# Revit family: Plymold-Essentials-Recycle_Receptacle-
name_source: partatom
category: Furniture
units: mm (PartAtom-declared; Revit-internal decimal feet)

## family parameters
Always vertical = Yes
Cut with Voids When Loaded = No
OmniClass Number = 23.40.20.00
OmniClass Title = General Furniture and Specialties
Render Appearance Source = Family Geometry
Room Calculation Point = No
Shared = No
Work Plane-Based = No

## types (1)
- 80140
    Assembly Code = E2020200
    BACK MATERIAL = PLY - Natural Maple Horizontal
    Brand = Receptacle
    Cost = 0 $
    DIVIDER MATERIAL = PLY - Natural Maple Vertical
    DOOR MATERIAL = PLY - Natural Maple Vertical
    Default Elevation = 0"
    Depth = 16 3/4"
    Description = Three Stream Recycle Receptacle - 49"W x 16 3/4"D x 42"H
    EDGE HORIZONTAL MATERIAL = PLY - Natural Maple Horizontal
    EDGE MATERIAL = PLY - Plastic Black
    EDGE VERTICAL MATERIAL = PLY - Natural Maple Vertical
    FRONT MATERIAL = PLY - Natural Maple Horizontal
    GLIDES MATERIAL = PLY - Plastic Black
    HANDLE MATERIAL = PLY - Plastic Black
    HARDWARE MATERIAL = PLY - Onyx Black Powdercoat
    Height = 42"
    Keynote = 12500
    LINER MATERIAL = PLY - Plastic Black
    Manufacturer = Plymold
    Model = 80140
    PULL MATERIAL = PLY - Metal_Galvanized
    Product Documentation Link = https://plymold.com
    Revit Model Built By = https://www.servex-us.com
    SIDE MATERIAL = PLY - Natural Maple Vertical
    Sustainability = https://plymold.com
    TOP MATERIAL = PLY - Natural Maple Horizontal
    Type Comments = Casegoods
    URL = https://plymold.com
    Width = 49"

## geometry (parser evidence)
native form markers: Sweep x4
no freeform markers — native parametric forms only
